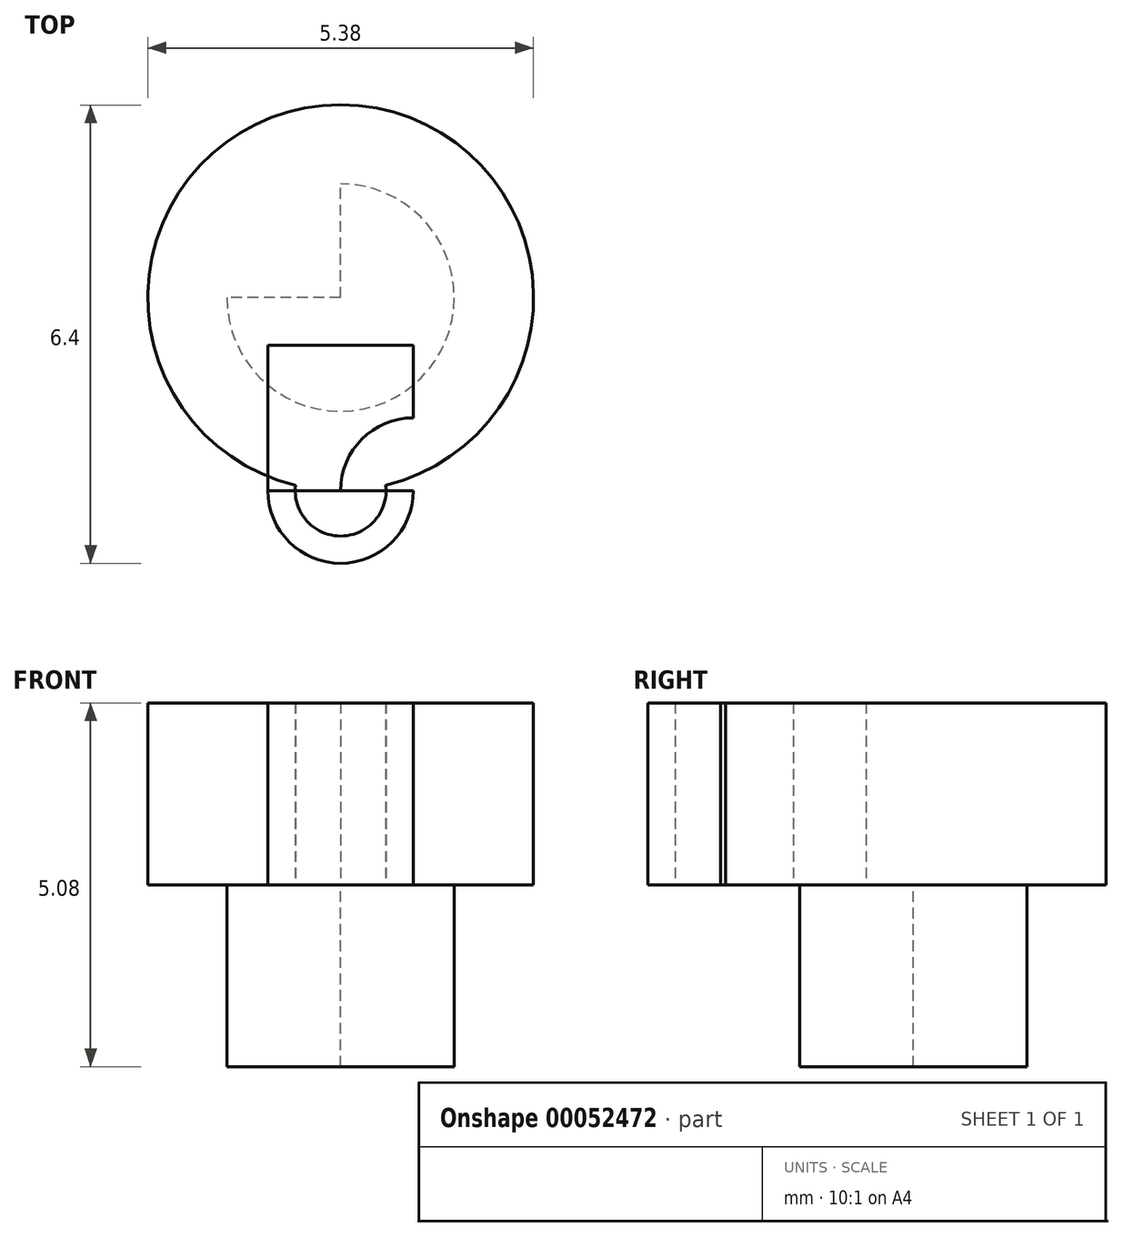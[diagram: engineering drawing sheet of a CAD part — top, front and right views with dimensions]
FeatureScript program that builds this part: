
annotation { "Feature Type Name" : "Feature", "Feature Type Description" : "" }
export const myFeature = defineFeature(function(context is Context, id is Id, definition is map)
    precondition{}
    {
        {
            var Q0;
            Q0=qCreatedBy(makeId("Top.planeOp"),FACE);
            var sketch = newSketch(context, id + "F0", { "sketchPlane" : qUnion([Q0])});
            skArc(sketch, "E0", {"start": v(-1.59, 0) * mm, "mid": v(1.12, -1.12) * mm, "end": v(0, 1.59) * mm});
            skLineSegment(sketch, "E1.bottom", {"start": v(0, 0) * mm, "end": v(-1.59, 0) * mm});
            skLineSegment(sketch, "E1.left", {"start": v(0, 0) * mm, "end": v(0, 1.59) * mm});
            skSolve(sketch);
        }
        {
            var Q0;
            Q0=qSketchRegion(id+"F0",true);
            extrude(context, id + "F1", {"entities" : qUnion([Q0]), "oppositeDirection" : true, "depth" : 2.54 * mm});
        }
        {
            var Q0;
            Q0=qCreatedBy(makeId("Top.planeOp"),FACE);
            var sketch = newSketch(context, id + "F2", { "sketchPlane" : qUnion([Q0])});
            skArc(sketch, "E2", {"start": v(0.63, -2.62) * mm, "mid": v(0, 2.7) * mm, "end": v(-0.63, -2.62) * mm});
            skArc(sketch, "E3", {"start": v(-0.63, -2.62) * mm, "mid": v(0, -3.33) * mm, "end": v(0.63, -2.62) * mm});
            skSolve(sketch);
        }
        {
            var Q0;
            Q0=qSketchRegion(id+"F2",true);
            extrude(context, id + "F3", {"entities" : qUnion([Q0]), "depth" : 2.54 * mm});
        }
        {
            var Q0;
            Q0=qCreatedBy(makeId("Top.planeOp"),FACE);
            var sketch = newSketch(context, id + "F4", { "sketchPlane" : qUnion([Q0])});
            skArc(sketch, "E4", {"start": v(-1.02, -2.7) * mm, "mid": v(0, -3.71) * mm, "end": v(1.02, -2.7) * mm});
            skLineSegment(sketch, "E5", {"start": v(1.02, -2.7) * mm, "end": v(-1.02, -2.7) * mm});
            skSolve(sketch);
        }
        {
            var Q0;
            Q0=qSketchRegion(id+"F4",true);
            extrude(context, id + "F5", {"entities" : qUnion([Q0]), "depth" : 2.54 * mm});
        }
        {
            var Q0;
            Q0=qCreatedBy(makeId("Top.planeOp"),FACE);
            var sketch = newSketch(context, id + "F6", { "sketchPlane" : qUnion([Q0])});
            skLineSegment(sketch, "E6.bottom", {"start": v(-1.02, -2.7) * mm, "end": v(0, -2.7) * mm});
            skLineSegment(sketch, "E6.top", {"start": v(-1.02, -0.66) * mm, "end": v(1.02, -0.66) * mm});
            skLineSegment(sketch, "E6.left", {"start": v(-1.02, -2.7) * mm, "end": v(-1.02, -0.66) * mm});
            skLineSegment(sketch, "E6.right", {"start": v(1.02, -1.68) * mm, "end": v(1.02, -0.66) * mm});
            skArc(sketch, "E7", {"start": v(1.02, -1.68) * mm, "mid": v(0.3, -1.98) * mm, "end": v(0, -2.7) * mm});
            skSolve(sketch);
        }
        {
            var Q0;
            Q0=makeQuery(id+"F6.imprint","IMPRINT",FACE,{"disambiguationData":[TD([[makeQuery(id+"F6.imprint","IMPRINT",EDGE,{"derivedFrom":sQuery(id+"F6.wireOp",EDGE,"E6.bottom")}),1.0]])]});
            extrude(context, id + "F7", {"entities" : qUnion([Q0]), "depth" : 2.54 * mm});
        }
    });
